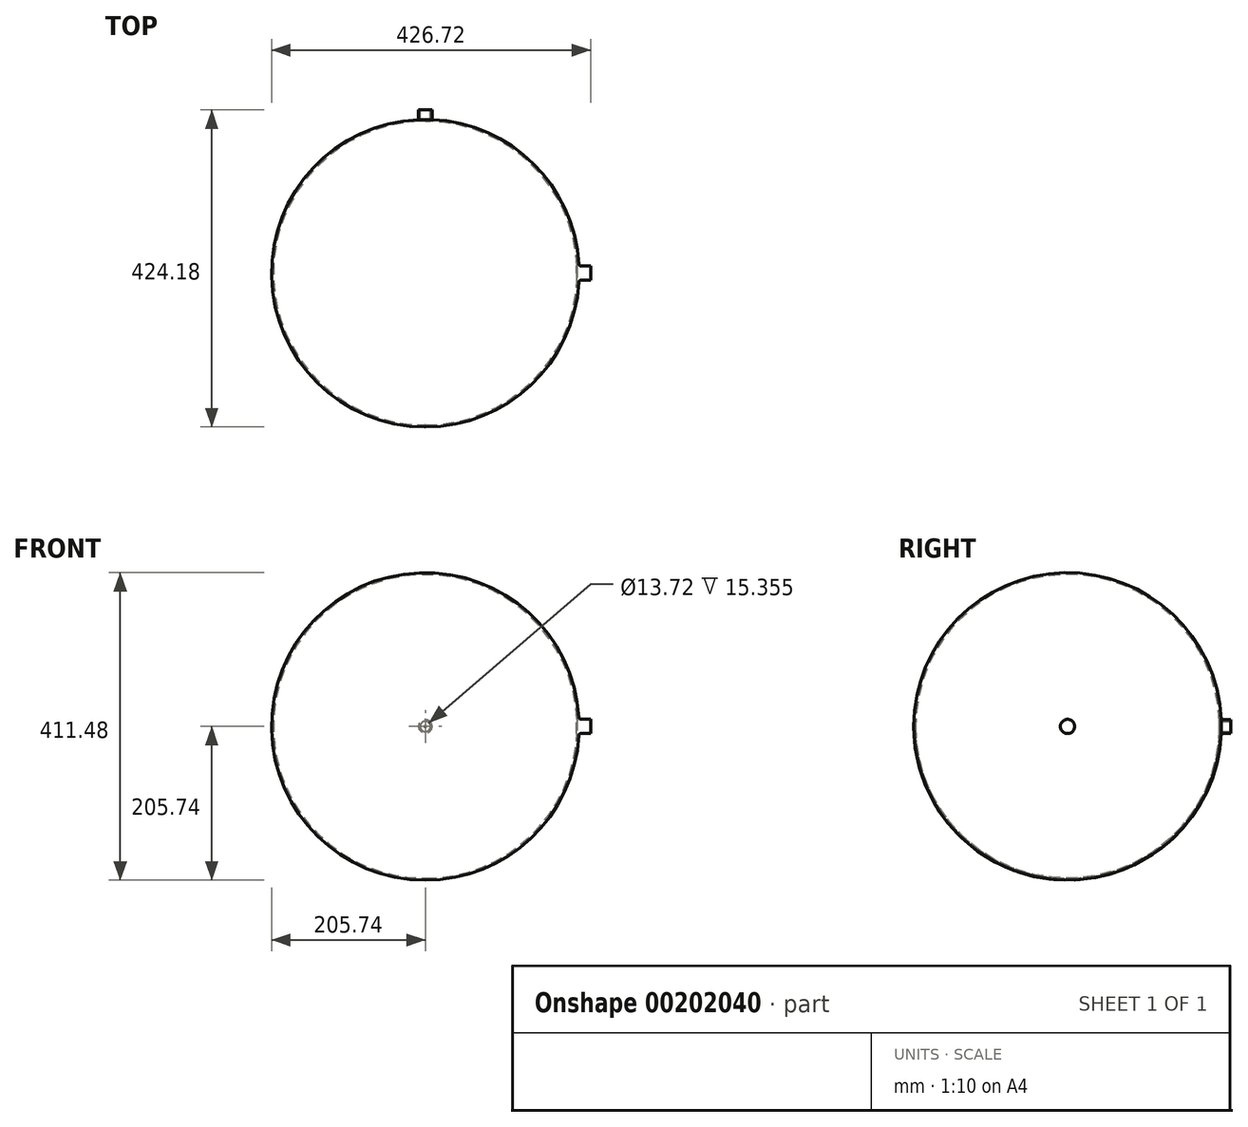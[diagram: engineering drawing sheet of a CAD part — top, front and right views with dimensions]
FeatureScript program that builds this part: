
annotation { "Feature Type Name" : "Feature", "Feature Type Description" : "" }
export const myFeature = defineFeature(function(context is Context, id is Id, definition is map)
    precondition{}
    {
        {
            var Q0;
            Q0=qCreatedBy(makeId("Top.planeOp"),FACE);
            var sketch = newSketch(context, id + "F0", { "sketchPlane" : qUnion([Q0])});
            skLineSegment(sketch, "E0", {"start": v(0, 0) * mm, "end": v(203.2, 0) * mm});
            skArc(sketch, "E1", {"start": v(0.55, -203.2) * mm, "mid": v(203.2, 0.27) * mm, "end": v(0, 203.2) * mm});
            skArc(sketch, "E2.0", {"start": v(0.55, -205.74) * mm, "mid": v(139.2, -151.5) * mm, "end": v(204.96, -17.94) * mm});
            skLineSegment(sketch, "E3", {"start": v(0.55, -205.74) * mm, "end": v(0.55, -203.2) * mm});
            skLineSegment(sketch, "E4", {"start": v(0, 0) * mm, "end": v(0, 127) * mm});
            skArc(sketch, "E5.trimOffspring", {"start": v(204.96, 17.94) * mm, "mid": v(142.27, 148.62) * mm, "end": v(8.97, 205.54) * mm});
            skLineSegment(sketch, "E6", {"start": v(0, 218.44) * mm, "end": v(8.97, 218.44) * mm});
            skLineSegment(sketch, "E7", {"start": v(8.97, 218.44) * mm, "end": v(8.97, 205.54) * mm});
            skLineSegment(sketch, "E8.trimOffspring", {"start": v(0, 203.2) * mm, "end": v(0, 218.44) * mm});
            skArc(sketch, "E9", {"start": v(0.55, -205.74) * mm, "mid": v(205.74, 0.28) * mm, "end": v(0, 205.74) * mm});
            skSolve(sketch);
        }
        {
            var Q0;
            {var subQ0=sQuery(id+"F0.wireOp",EDGE,"E6");Q0=makeQuery(id+"F0.imprint","IMPRINT",FACE,{"disambiguationData":[TD([[makeQuery(id+"F0.imprint","IMPRINT",EDGE,{"derivedFrom":subQ0}),-1.0]])]});}
            var Q1;
            {var subQ5=sQuery(id+"F0.wireOp",EDGE,"E3");Q1=makeQuery(id+"F0.imprint","IMPRINT",FACE,{"disambiguationData":[TD([[makeQuery(id+"F0.imprint","IMPRINT",EDGE,{"derivedFrom":subQ5}),-1.0]])]});}
            var Q2;
            Q2=sQuery(id+"F0.wireOp",EDGE,"E4");
            revolve(context, id + "F1", {"entities" : qUnion([Q0, Q1]), "axis" : qUnion([Q2]), "revolveType" : RevolveType.FULL});
        }
        {
            var Q0;
            Q0=makeQuery(id+"F1.opRevolve","SWEPT_FACE",FACE,{"disambiguationData":[OSD([sQuery(id+"F0.wireOp",EDGE,"E6")])]});
            var sketch = newSketch(context, id + "F2", { "sketchPlane" : qUnion([Q0])});
            skCircle(sketch, "E10", {"center": v(0, 0) * mm, "radius": 6.86 * mm});
            skSolve(sketch);
        }
        {
            var Q0;
            Q0=makeQuery(id+"F2.imprint","IMPRINT",FACE,{"disambiguationData":[TD([[makeQuery(id+"F2.imprint","IMPRINT",EDGE,{"derivedFrom":sQuery(id+"F2.wireOp",EDGE,"E10")}),1.0]])]});
            extrude(context, id + "F3", {"entities" : qUnion([Q0]), "operationType" : NewBodyOperationType.REMOVE, "oppositeDirection" : true, "depth" : 25.4 * mm});
        }
        {
            var Q0;
            Q0=sQuery(id+"F0.wireOp",EDGE,"E0");
            cPlane(context, id + "F4", {"entities" : qUnion([Q0]), "cplaneType" : CPlaneType.LINE_ANGLE, "offset" : 25.4 * mm, "angle" : 0 * degree, "width" : 152.4 * mm, "height" : 152.4 * mm});
        }
        {
            var Q0;
            Q0=qCreatedBy(id+"F4.planeOp",FACE);
            var sketch = newSketch(context, id + "F5", { "sketchPlane" : qUnion([Q0])});
            skLineSegment(sketch, "E11", {"start": v(-205.74, 0) * mm, "end": v(-205.74, 154.5) * mm});
            skSolve(sketch);
        }
        {
            var Q0;
            Q0=sQuery(id+"F5.wireOp",EDGE,"E11");
            cPlane(context, id + "F6", {"entities" : qUnion([Q0]), "cplaneType" : CPlaneType.LINE_ANGLE, "offset" : 25.4 * mm, "angle" : 0 * degree, "width" : 152.4 * mm, "height" : 152.4 * mm});
        }
        {
            var Q0;
            Q0=qCreatedBy(id+"F6.planeOp",FACE);
            var sketch = newSketch(context, id + "F7", { "sketchPlane" : qUnion([Q0])});
            skCircle(sketch, "E12", {"center": v(0, 0) * mm, "radius": 9.53 * mm});
            skSolve(sketch);
        }
        {
            var Q0;
            Q0=makeQuery(id+"F7.imprint","IMPRINT",FACE,{"disambiguationData":[TD([[makeQuery(id+"F7.imprint","IMPRINT",EDGE,{"derivedFrom":sQuery(id+"F7.wireOp",EDGE,"E12")}),1.0]])]});
            extrude(context, id + "F8", {"entities" : qUnion([Q0]), "operationType" : NewBodyOperationType.ADD, "depth" : 15.24 * mm, "hasSecondDirection" : true, "secondDirectionOppositeDirection" : true, "secondDirectionDepth" : 3.56 * mm});
        }
        {
            var Q0;
            Q0=makeQuery(id+"F8.boolean.opBoolean","INTERSECT",EDGE,{"derivedFrom":[makeQuery(id+"F1.opRevolve","SWEPT_FACE",FACE,{"disambiguationData":[OSD([sQuery(id+"F0.wireOp",EDGE,"E9")])]}),makeQuery(id+"F8.opExtrude","SWEPT_FACE",FACE,{"disambiguationData":[OSD([sQuery(id+"F7.wireOp",EDGE,"E12")])]})]});
            fillet(context, id + "F9", {"entities" : qUnion([Q0]), "radius" : 2.54 * mm, "tangentPropagation" : true, "allowEdgeOverflow" : false});
        }
    });
